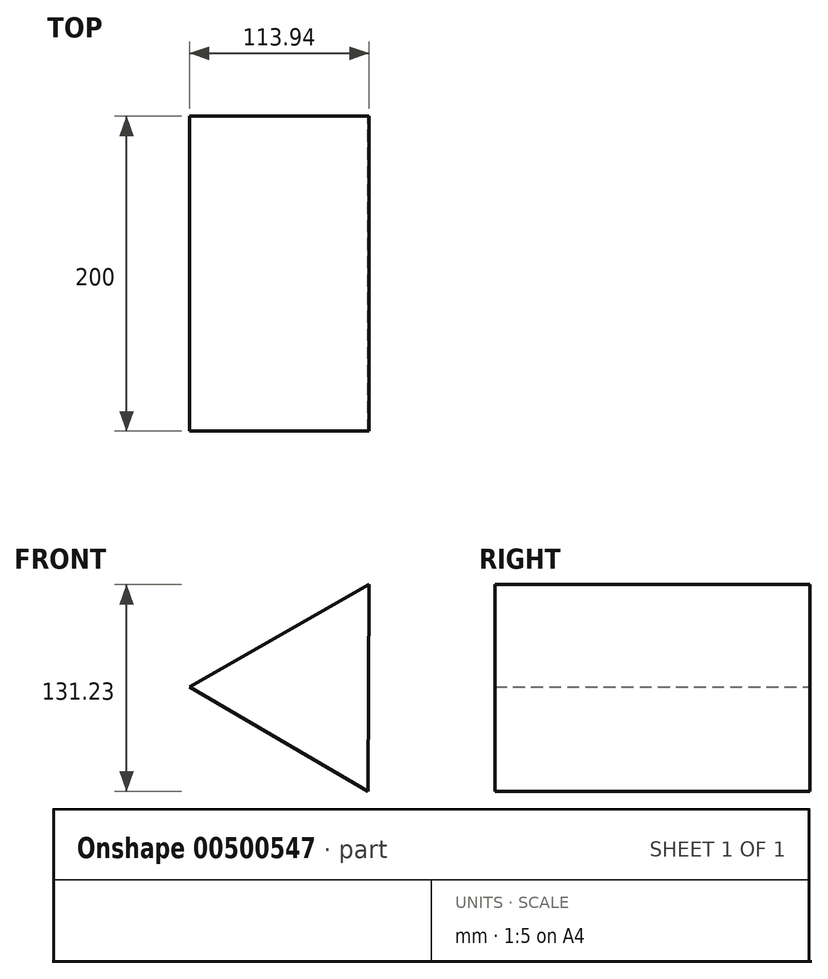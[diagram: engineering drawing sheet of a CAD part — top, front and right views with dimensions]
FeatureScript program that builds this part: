
annotation { "Feature Type Name" : "Feature", "Feature Type Description" : "" }
export const myFeature = defineFeature(function(context is Context, id is Id, definition is map)
    precondition{}
    {
        {
            var Q0;
            Q0=qCreatedBy(makeId("Front.planeOp"),FACE);
            var sketch = newSketch(context, id + "F0", { "sketchPlane" : qUnion([Q0])});
            skCircle(sketch, "E0.cCircle", {"center": v(0, 0) * mm, "radius": 75.76 * mm, "construction": true});
            skLineSegment(sketch, "E0.0", {"start": v(38.18, 65.44) * mm, "end": v(37.58, -65.79) * mm});
            skLineSegment(sketch, "E0.1", {"start": v(37.58, -65.79) * mm, "end": v(-75.76, 0.35) * mm});
            skLineSegment(sketch, "E0.2", {"start": v(-75.76, 0.35) * mm, "end": v(38.18, 65.44) * mm});
            skSolve(sketch);
        }
        {
            var Q0;
            Q0=makeQuery(id+"F0.imprint","IMPRINT",FACE,{"disambiguationData":[TD([[makeQuery(id+"F0.imprint","IMPRINT",EDGE,{"derivedFrom":sQuery(id+"F0.wireOp",EDGE,"E0.0")}),-1.0]])]});
            extrude(context, id + "F1", {"entities" : qUnion([Q0]), "depth" : 200 * mm});
        }
    });
